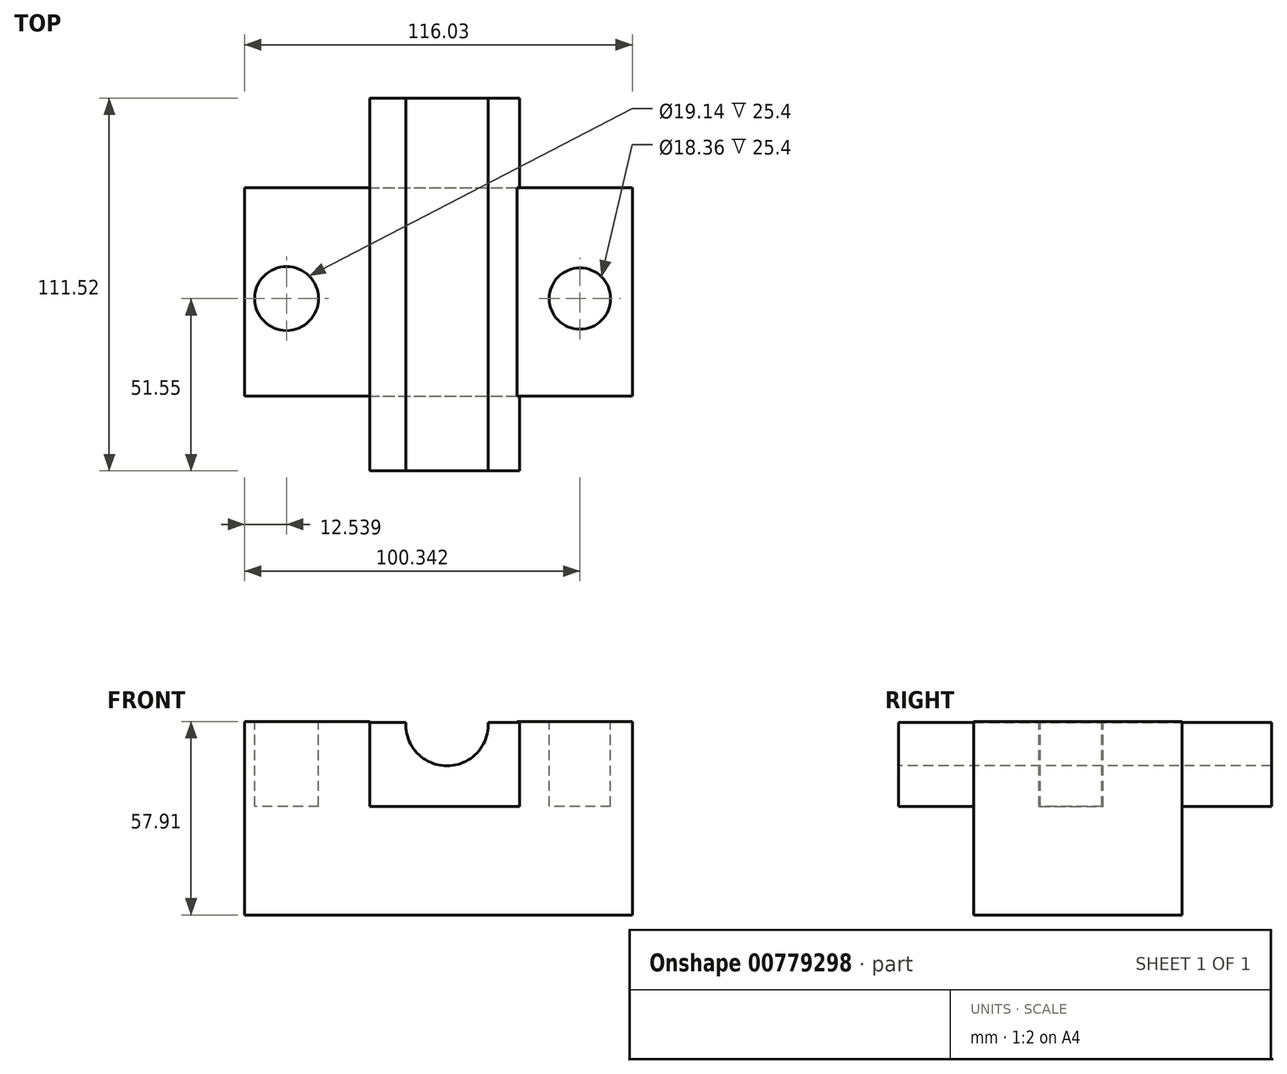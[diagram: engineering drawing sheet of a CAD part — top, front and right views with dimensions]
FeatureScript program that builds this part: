
annotation { "Feature Type Name" : "Feature", "Feature Type Description" : "" }
export const myFeature = defineFeature(function(context is Context, id is Id, definition is map)
    precondition{}
    {
        {
            var Q0;
            Q0=qCreatedBy(makeId("Top.planeOp"),FACE);
            var sketch = newSketch(context, id + "F0", { "sketchPlane" : qUnion([Q0])});
            skLineSegment(sketch, "E0.bottom", {"start": v(-56.9, 33.17) * mm, "end": v(59.12, 33.17) * mm});
            skLineSegment(sketch, "E0.top", {"start": v(-56.9, -29.16) * mm, "end": v(59.12, -29.16) * mm});
            skLineSegment(sketch, "E0.left", {"start": v(-56.9, 33.17) * mm, "end": v(-56.9, -29.16) * mm});
            skLineSegment(sketch, "E0.right", {"start": v(59.12, 33.17) * mm, "end": v(59.12, -29.16) * mm});
            skSolve(sketch);
        }
        {
            var Q0;
            Q0 = qSketchRegion(id + "F0", true);
            extrude(context, id + "F1", {"entities" : qUnion([Q0]), "depth" : 57.9 * mm, "offsetDistance" : 25.4 * mm});
        }
        {
            var Q0;
            Q0=makeQuery(id+"F1.opExtrude","CAP_FACE",FACE,{"disambiguationData":[OSD([sQuery(id+"F0.wireOp",EDGE,"E0.bottom"),sQuery(id+"F0.wireOp",EDGE,"E0.top"),sQuery(id+"F0.wireOp",EDGE,"E0.left"),sQuery(id+"F0.wireOp",EDGE,"E0.right")])],"isStart":false});
            var sketch = newSketch(context, id + "F2", { "sketchPlane" : qUnion([Q0])});
            skCircle(sketch, "E1", {"center": v(43.43, 0) * mm, "radius": 9.18 * mm});
            skCircle(sketch, "E2", {"center": v(-44.37, 0) * mm, "radius": 9.57 * mm});
            skSolve(sketch);
        }
        {
            var Q0;
            Q0 = qSketchRegion(id + "F2", true);
            extrude(context, id + "F3", {"entities" : qUnion([Q0]), "operationType" : NewBodyOperationType.REMOVE, "oppositeDirection" : true, "depth" : 25.4 * mm, "offsetDistance" : 25.4 * mm});
        }
        {
            var Q0;
            Q0=makeQuery(id+"F1.opExtrude","CAP_FACE",FACE,{"disambiguationData":[OSD([sQuery(id+"F0.wireOp",EDGE,"E0.bottom"),sQuery(id+"F0.wireOp",EDGE,"E0.top"),sQuery(id+"F0.wireOp",EDGE,"E0.left"),sQuery(id+"F0.wireOp",EDGE,"E0.right")])],"isStart":false});
            var sketch = newSketch(context, id + "F4", { "sketchPlane" : qUnion([Q0])});
            skLineSegment(sketch, "E3.bottom", {"start": v(-19.5, 59.48) * mm, "end": v(24.57, 59.48) * mm});
            skLineSegment(sketch, "E3.top", {"start": v(-19.5, -59.92) * mm, "end": v(24.57, -59.92) * mm});
            skLineSegment(sketch, "E3.left", {"start": v(-19.5, 59.48) * mm, "end": v(-19.5, -59.92) * mm});
            skLineSegment(sketch, "E3.right", {"start": v(24.57, 59.48) * mm, "end": v(24.57, -59.92) * mm});
            skSolve(sketch);
        }
        {
            var Q0;
            Q0 = qSketchRegion(id + "F4", true);
            extrude(context, id + "F5", {"entities" : qUnion([Q0]), "operationType" : NewBodyOperationType.REMOVE, "oppositeDirection" : true, "depth" : 25.4 * mm, "offsetDistance" : 25.4 * mm});
        }
        {
            var Q0;
            Q0=makeQuery(id+"F5.boolean.opBoolean","COPY",FACE,{"derivedFrom":makeQuery(id+"F5.opExtrude","CAP_FACE",FACE,{"disambiguationData":[OSD([sQuery(id+"F4.wireOp",EDGE,"E3.bottom"),sQuery(id+"F4.wireOp",EDGE,"E3.top"),sQuery(id+"F4.wireOp",EDGE,"E3.left"),sQuery(id+"F4.wireOp",EDGE,"E3.right")])],"isStart":false})});
            var sketch = newSketch(context, id + "F6", { "sketchPlane" : qUnion([Q0])});
            skLineSegment(sketch, "E4.bottom", {"start": v(25.32, -51.55) * mm, "end": v(-19.5, -51.55) * mm});
            skLineSegment(sketch, "E4.top", {"start": v(25.32, 59.97) * mm, "end": v(-19.5, 59.97) * mm});
            skLineSegment(sketch, "E4.left", {"start": v(25.32, -51.55) * mm, "end": v(25.32, 59.97) * mm});
            skLineSegment(sketch, "E4.right", {"start": v(-19.5, -51.55) * mm, "end": v(-19.5, 59.97) * mm});
            skSolve(sketch);
        }
        {
            var Q0;
            Q0 = qSketchRegion(id + "F6", true);
            extrude(context, id + "F7", {"entities" : qUnion([Q0]), "operationType" : NewBodyOperationType.ADD, "depth" : 25.15 * mm, "offsetDistance" : 25.4 * mm});
        }
        {
            var Q0;
            Q0=makeQuery(id+"F7.opExtrude","SWEPT_FACE",FACE,{"disambiguationData":[OSD([sQuery(id+"F6.wireOp",EDGE,"E4.bottom")])]});
            var sketch = newSketch(context, id + "F8", { "sketchPlane" : qUnion([Q0])});
            skArc(sketch, "E5", {"start": v(-8.68, 57.66) * mm, "mid": v(3.63, 44.62) * mm, "end": v(15.94, 57.66) * mm});
            skSolve(sketch);
        }
        {
            var Q0;
            {var subQ0=sQuery(id+"F8.wireOp",EDGE,"E5");Q0=makeQuery(id+"F8.imprint","IMPRINT",FACE,{"disambiguationData":[TD([[makeQuery(id+"F8.imprint","IMPRINT",EDGE,{"derivedFrom":subQ0}),1.0]])]});}
            extrude(context, id + "F9", {"entities" : qUnion([Q0]), "operationType" : NewBodyOperationType.REMOVE, "oppositeDirection" : true, "depth" : 139.45 * mm, "offsetDistance" : 25.4 * mm});
        }
    });
